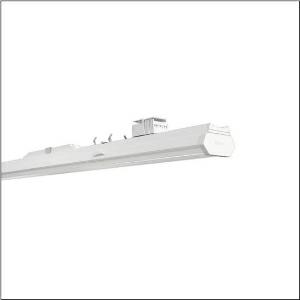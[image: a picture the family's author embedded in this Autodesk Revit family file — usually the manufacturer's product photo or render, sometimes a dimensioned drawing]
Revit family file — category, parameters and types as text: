
# Revit family: licross_r__21_protected_ho_52td11mn4fxs_06ba
name_source: partatom
category: Lighting Fixtures
units: mm (PartAtom-declared; Revit-internal decimal feet)

## family parameters
Cut with Voids When Loaded = No
Host = Face
Light Source = No
Part Type = Normal
Room Calculation Point = No
Round Connector Dimension = Use Diameter
Shared = No

## types (1)
- --- (1 x LED, 15020 lm, 83.2 W, 4000K)
    Apparent Load = 83 VA
    CIE Flux Codes = 84 94 98 99 100
    Color Rendering = 80
    Color Temperature = 4000K
    Default Elevation = 1800 mm
    Description = Licross® 21 Protected HO, luminaire insert, of sheet steel, galvanised, coil coated, white, length: 1.500mm, width: 66mm, height: 67mm, LED rated luminous flux: 15.020lm, light colour: 840, control gear: ON/OFF Multilumen, with plug, 3-pole, with phase selection, mains connection: 220..240V, AC, 50/60Hz, rated input power: 83W, internal wiring halogen-free, primary light control with lens, of plastic, primary optical cover: cover, of PMMA, light emission: direct distribution, primary light characteristic: symmetric, protection rating (complete): IP54, insulation class (complete): insulation class I (protective earthing), certification: CE, ENEC, VDE, UKCA, protection symbol: D if used in an environment with non-conductive dust loads with corresponding accessories, impact resistance: IK06, permissible ambient temperature for indoor applications: -35..+35°C, corresponds to IFS (International Featured Standards) requirements for safety and quality in the food industry, reducing of maximum allowable ambient temperature of 5°C with ceiling mounting, LABS conformity tested according to VDMA 24364:2018-05, packaging unit: 1 piece
    Height = 92 mm
    Lamp = 1 x LED
    Lamp Light Flux = 15020 lm
    Lamp Power = 83.2 W
    Lamp count = 1
    Length = 1500 mm
    Luminous efficacy = 181 lm/W
    Manufacturer = Siteco
    ModVariant = No
    Model = 52TD11MN4FXS
    Mounting Place = Ceiling
    Mounting Type = Pendant
    Number of Poles = 1
    OnlyDefault = Yes
    Power Factor = 1
    Product Name = Licross® 21 Protected HO
    Product group = luminaire insert | ceiling pendant
    ProductGroupID = 902
    Protection Class = Protection class I
    Protection Degree = IP 54
    RLX_Detail_Level = 1
    RLX_Emergency_Light_Flux = 0 lm
    RLX_Emergency_Type = 0
    RLX_Emergency_Type_DB = No
    RlxData = <blob elided: 21949 chars, md5=b71672f9>
    Socket = socket
    Standby Power = 0 W
    System Light Flux = 15020 lm
    System Power = 83 W
    Type Comments = factory setting: luminous flux: 100 % | (A | C | E) | 195 mA
    Type Image = l_1256148.jpg
    URL = http://relux.com
    VarID = @adj_130543
    Voltage = 0 V
    Weight = 0.00 kg
    Width = 88 mm

## geometry (parser evidence)
native form markers: Blend x4, Sweep x9
no freeform markers — native parametric forms only
